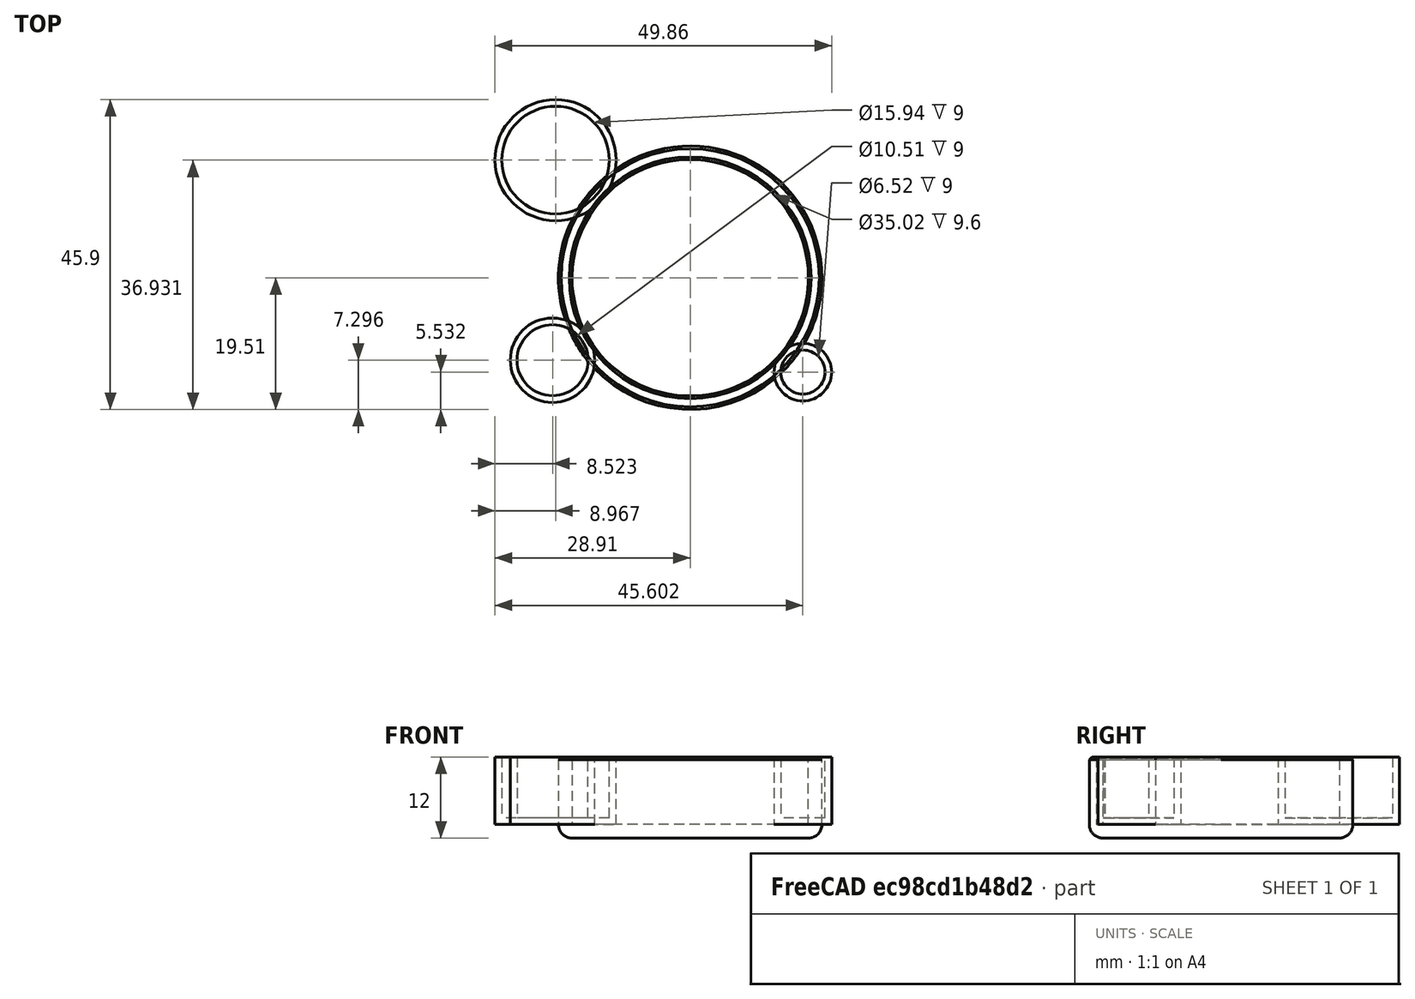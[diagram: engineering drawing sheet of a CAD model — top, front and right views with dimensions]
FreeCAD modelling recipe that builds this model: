
FCSTD DOCUMENT  (FreeCAD 1.1R38843 (Git))
Label: test
License: All rights reserved
LicenseURL: http://en.wikipedia.org/wiki/All_rights_reserved
objects: Sketcher::SketchObject×2, PartDesign::Pad×2, PartDesign::Thickness×2, PartDesign::Body×2, PartDesign::Chamfer×1, PartDesign::SubShapeBinder×1
note: 22 computed .brp shape members not serialized (recipe doc carries the construction recipe); baked Part::Feature solids carry a one-line shape summary decoded from their .brp

FEATURE [Sketcher::SketchObject] Sketch
  ArcFitTolerance = 1e-06
  AttachmentSupport = -> [XY_Plane]
  FullyConstrained = false
  MakeInternals = false
  MapMode = 5
  sketch-geometry (1):
    g0: Circle CenterX=0 CenterY=0 CenterZ=0 NormalX=0 NormalY=0 NormalZ=1 AngleXU=0 Radius=17.512
  constraints (1):
    c: Coincident(g0,g-1)
FEATURE [PartDesign::Pad] Pad
  Direction = (0,0,1)
  Length = 10
  Length2 = 10
  Profile = -> Sketch
  ReferenceAxis = -> Sketch [N_Axis]
  Refine = true
  Suppressed = false
  Type = 0
FEATURE [PartDesign::Thickness] Thickness
  Base = -> Pad [Face3]
  BaseFeature = -> Pad
  Intersection = false
  Join = 0
  Mode = 0
  Refine = true
  SupportTransform = false
  Suppressed = false
  Value = 2
FEATURE [PartDesign::Chamfer] Chamfer
  Angle = 45
  Base = -> Thickness [Face3]
  BaseFeature = -> Thickness
  ChamferType = 0
  FlipDirection = false
  Refine = true
  Size = 0.4
  Size2 = 1
  SupportTransform = false
  Suppressed = false
  UseAllEdges = false
FEATURE [PartDesign::Body] Body
  AllowCompound = false
  Group = -> [Sketch,Pad,Thickness,Chamfer]
  Origin = -> Origin
  Tip = -> Chamfer
FEATURE [PartDesign::SubShapeBinder] Binder
  BindCopyOnChange = 0
  BindMode = 0
  ClaimChildren = false
  Context = -> Body001 [Binder.]
  Fuse = false
  MakeFace = true
  OffsetFill = false
  OffsetIntersection = false
  OffsetJoinType = 0
  OffsetOpenResult = false
  PartialLoad = false
  Refine = true
  Relative = true
  Support = -> [Body[Sketch.]]
  _Version = 2
FEATURE [Sketcher::SketchObject] Sketch001
  ArcFitTolerance = 1e-06
  AttachmentSupport = -> [XY_Plane001]
  ExternalGeometry = -> [Binder]
  FullyConstrained = false
  MakeInternals = false
  MapMode = 5
  sketch-geometry (3):
    g0: Circle CenterX=-19.9433 CenterY=17.4212 CenterZ=0 NormalX=0 NormalY=0 NormalZ=1 AngleXU=0 Radius=8.96883
    g1: Circle CenterX=-20.3873 CenterY=-12.2142 CenterZ=0 NormalX=0 NormalY=0 NormalZ=1 AngleXU=0 Radius=6.25419
    g2: Circle CenterX=16.6925 CenterY=-13.9783 CenterZ=0 NormalX=0 NormalY=0 NormalZ=1 AngleXU=0 Radius=4.2603
  constraints (3):
    c: Tangent(g2,g-3)
    c: Tangent(g1,g-3)
    c: Tangent(g0,g-3)
FEATURE [PartDesign::Pad] Pad001
  Direction = (0,0,1)
  Length = 10
  Length2 = 10
  Profile = -> Sketch001
  ReferenceAxis = -> Sketch001 [N_Axis]
  Refine = true
  Suppressed = false
  Type = 0
FEATURE [PartDesign::Thickness] Thickness001
  Base = -> Pad001 [Face3,Face6,Face9]
  BaseFeature = -> Pad001
  Intersection = false
  Join = 0
  Mode = 0
  Refine = true
  Reversed = true
  SupportTransform = false
  Suppressed = false
  Value = 1
FEATURE [PartDesign::Body] Body001
  AllowCompound = true
  Group = -> [Sketch001,Binder,Pad001,Thickness001]
  Origin = -> Origin001
  Tip = -> Thickness001
